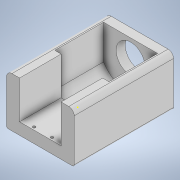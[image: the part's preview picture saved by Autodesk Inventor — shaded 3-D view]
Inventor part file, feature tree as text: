
AUTODESK INVENTOR PART (.ipt)
format: ipt  version: 2022 (Build 260153000, 153)  size: 245,760 bytes
history: native  units: mm
features: sketch x13, extrude x11, fillet x2, hole x1
ambient origin geometry x8: Origin, YZ Plane, XZ Plane, XY Plane, X Axis, Y Axis, Z Axis, Center Point
bodies: Solid1 (feature_tree)
feature tree (27):
  extrude  "Extrusion1"  Depth=75.0mm
  extrude  "Extrusion2"  Depth=8.0mm TaperAngle=0.0deg
  extrude  "Extrusion3"  Depth=42.0mm TaperAngle=0.0deg
  extrude  "Extrusion4"  Depth=36.056mm
  extrude  "Extrusion5"  Depth=30.0mm
  extrude  "Extrusion6"  Depth=18.028mm
  hole  "Hole2"  [1 undecoded]
  sketch  "Sketch9"  dims[d26=42.0mm d27=0.0mm d28=4.0mm d29=0.0mm]
  extrude  "Extrusion7"  Depth=42.0mm TaperAngle=0.0deg
  extrude  "Extrusion8"  Depth=10.0mm
  extrude  "Extrusion9"  Depth=10.0mm
  fillet  "Fillet2"  [1 undecoded]
  fillet  "Fillet3"  Radius=10.0mm
  extrude  "Extrusion10"  Depth=6.0mm
  extrude  "Extrusion11"  Depth=10.0mm TaperAngle=0.0deg
  sketch  "Sketch1"  dims[d0=75.0mm d1=91.0mm]
  sketch  "Sketch2"  dims[d2=5.0mm d3=0.0mm d10=8.0mm d11=0.0mm]
  sketch  "Sketch3"  dims[d12=15.0mm d13=0.0mm d16=42.0mm d17=0.0mm]
  sketch  "Sketch4"  dims[d18=18.028mm d19=36.056mm]
  sketch  "Sketch5"  dims[d20=30.0mm d21=30.0mm]
  sketch  "Sketch6"  dims[d22=30.0mm d23=18.028mm]
  sketch  "Sketch8"  dims[d24=18.028mm d25=35.0mm]
  sketch  "Sketch10"  dims[d43=3.0mm d44=6.0mm d45=5.0mm d46=2.0mm d47=90.0deg d48=8.0mm d49=20.594885mm d50=10.0mm]
  sketch  "Sketch11"  dims[d51=46.0mm d52=0.0mm d56=33.0mm d57=0.0mm d58=0.0mm d59=10.0mm d60=0.0mm]
  sketch  "Sketch12"  dims[d62=2.0mm d63=6.0mm]
  sketch  "Sketch13"  dims[d68=3.0mm d69=10.0mm d70=0.0mm]
  sketch  "Sketch14"  dims[d71=32.0mm d72=10.0mm d73=0.0mm d55=0.5mm]
note: 2 required parameter values undecoded (feature->parameter linkage not recoverable at this tier; creation-order binding heuristic only, values carry confidence <= 0.55)
